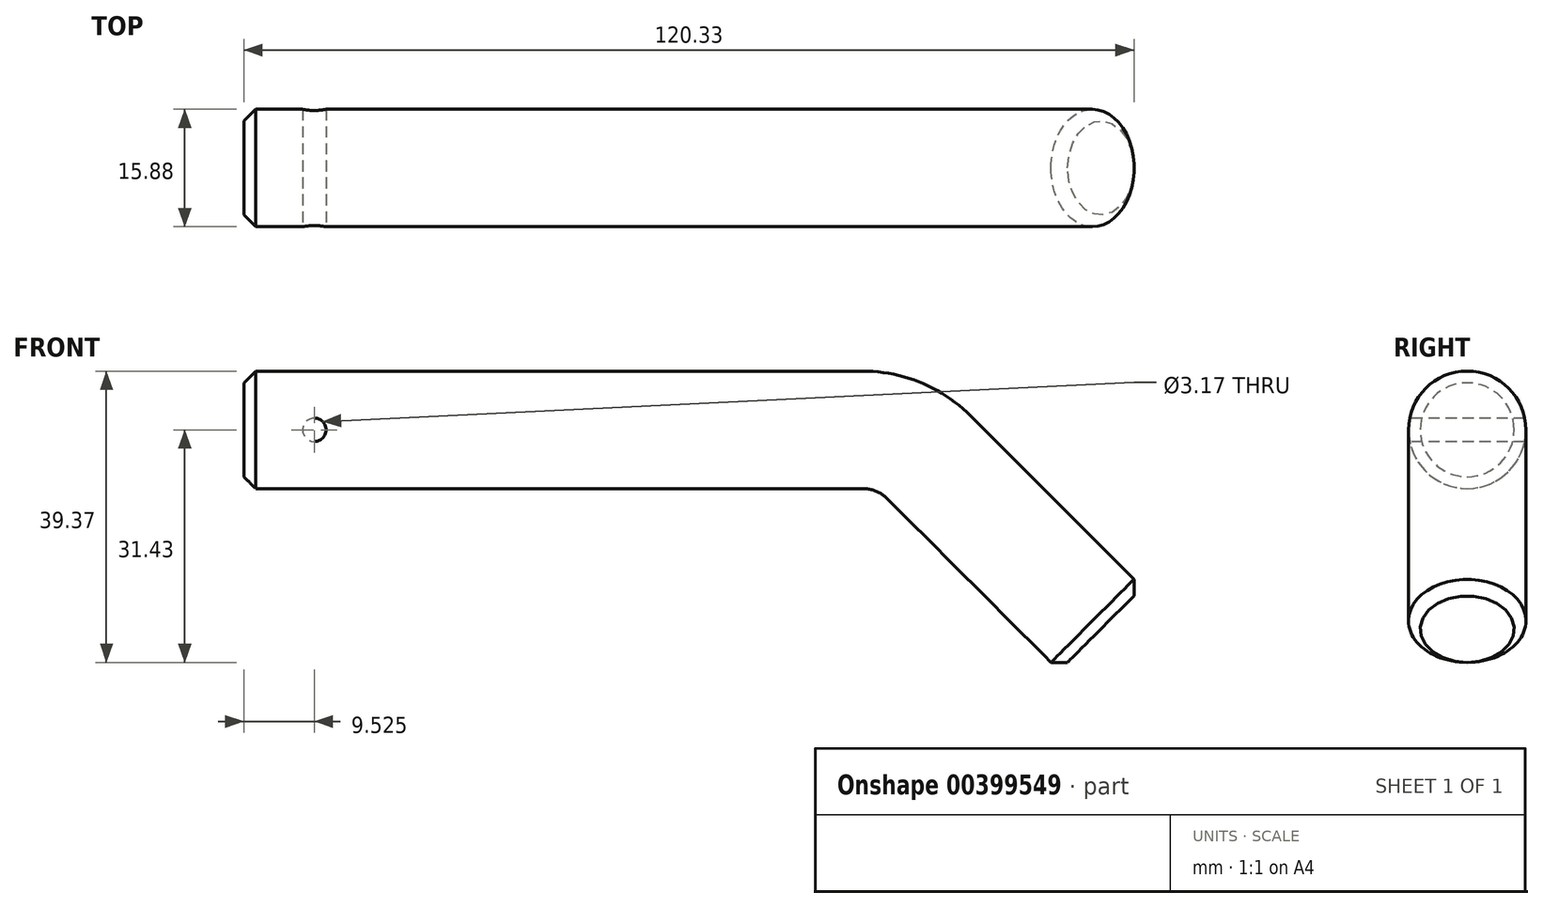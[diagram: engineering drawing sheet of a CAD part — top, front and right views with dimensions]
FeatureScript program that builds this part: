
annotation { "Feature Type Name" : "Feature", "Feature Type Description" : "" }
export const myFeature = defineFeature(function(context is Context, id is Id, definition is map)
    precondition{}
    {
        {
            var Q0;
            Q0=qCreatedBy(makeId("Front.planeOp"),FACE);
            var sketch = newSketch(context, id + "F0", { "sketchPlane" : qUnion([Q0])});
            skLineSegment(sketch, "E0", {"start": v(0, 0) * mm, "end": v(83.64, 0) * mm});
            skLineSegment(sketch, "E1", {"start": v(92.62, -3.72) * mm, "end": v(115.84, -26.94) * mm});
            skPoint(sketch, "E2.visualSharp", {"position": v(88.9, 0) * mm});
            skArc(sketch, "E2.filletArc", {"start": v(92.62, -3.72) * mm, "mid": v(88.5, -0.97) * mm, "end": v(83.64, 0) * mm});
            skSolve(sketch);
        }
        {
            var Q0;
            Q0=qCreatedBy(makeId("Right.planeOp"),FACE);
            var sketch = newSketch(context, id + "F1", { "sketchPlane" : qUnion([Q0])});
            skCircle(sketch, "E3", {"center": v(0, 0) * mm, "radius": 7.94 * mm});
            skSolve(sketch);
        }
        {
            var Q0;
            Q0=makeQuery(id+"F1.imprint","IMPRINT",FACE,{"disambiguationData":[TD([[makeQuery(id+"F1.imprint","IMPRINT",EDGE,{"derivedFrom":sQuery(id+"F1.wireOp",EDGE,"E3")}),1.0]])]});
            var Q1;
            Q1=sQuery(id+"F0.wireOp",EDGE,"E0");
            var Q2;
            Q2=sQuery(id+"F0.wireOp",EDGE,"E2.filletArc");
            var Q3;
            Q3=sQuery(id+"F0.wireOp",EDGE,"E1");
            sweep(context, id + "F2", {"profiles" : qUnion([Q0]), "path" : qUnion([Q1, Q2, Q3])});
        }
        {
            var Q0;
            Q0=qCreatedBy(makeId("Front.planeOp"),FACE);
            var sketch = newSketch(context, id + "F3", { "sketchPlane" : qUnion([Q0])});
            skLineSegment(sketch, "E4", {"start": v(0, 0) * mm, "end": v(9.53, 0) * mm});
            skSolve(sketch);
        }
        {
            var Q0;
            Q0=sQuery(id+"F3.wireOp",VERTEX,"E4.end");
            var Q1;
            Q1=makeQuery(id+"F2.opSweep","SWEPT_BODY",BODY,{"disambiguationData":[OSD([sQuery(id+"F0.wireOp",EDGE,"E1"),sQuery(id+"F1.wireOp",EDGE,"E3")])]});
            hole(context, id + "F4", {"style" : HoleStyle.SIMPLE, "endStyle" : HoleEndStyle.THROUGH, "holeDiameter" : 3.17 * mm, "locations" : qUnion([Q0]), "scope" : qUnion([Q1]), "isTappedThrough" : true});
        }
        {
            var Q0;
            Q0=sQuery(id+"F3.wireOp",VERTEX,"E4.end");
            var Q1;
            Q1=makeQuery(id+"F2.opSweep","SWEPT_BODY",BODY,{"disambiguationData":[OSD([sQuery(id+"F0.wireOp",EDGE,"E1"),sQuery(id+"F1.wireOp",EDGE,"E3")])]});
            hole(context, id + "F5", {"style" : HoleStyle.SIMPLE, "endStyle" : HoleEndStyle.THROUGH, "oppositeDirection" : true, "holeDiameter" : 3.17 * mm, "locations" : qUnion([Q0]), "scope" : qUnion([Q1]), "isTappedThrough" : true});
        }
        {
            var Q0;
            Q0=makeQuery(id+"F2.opSweep","CAP_EDGE",EDGE,{"disambiguationData":[OSD([sQuery(id+"F0.wireOp",VERTEX,"E0.start"),sQuery(id+"F1.wireOp",EDGE,"E3")])],"isStart":true});
            var Q1;
            Q1=makeQuery(id+"F2.opSweep","CAP_EDGE",EDGE,{"disambiguationData":[OSD([sQuery(id+"F0.wireOp",VERTEX,"E1.end"),sQuery(id+"F1.wireOp",EDGE,"E3")])],"isStart":false});
            chamfer(context, id + "F6", {"entities" : qUnion([Q0, Q1]), "width" : 1.59 * mm, "tangentPropagation" : true});
        }
    });
